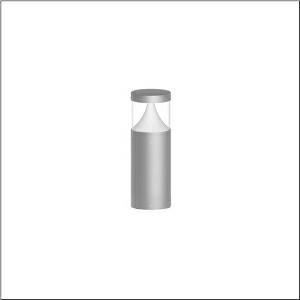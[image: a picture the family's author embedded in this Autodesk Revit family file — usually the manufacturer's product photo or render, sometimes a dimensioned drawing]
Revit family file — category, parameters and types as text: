
# Revit family: cl_31_poller_40_5cl424603
name_source: partatom
category: Lighting Fixtures
units: mm (PartAtom-declared; Revit-internal decimal feet)

## family parameters
Cut with Voids When Loaded = No
Host = Face
Light Source = No
Part Type = Normal
Room Calculation Point = No
Round Connector Dimension = Use Diameter
Shared = No

## types (1)
- --- (1 x LED, 800 lm, 7.2 W, 3000K)
    Apparent Load = 7 VA
    CIE Flux Codes = 19 66 88 92 100
    Color Rendering = 80
    Color Temperature = 3000K
    Default Elevation = 1800 mm
    Description = CL 31 Bollard 40, bollard luminaire, primary light control with lens, of PC, primary optical cover: cover panel, of PC, transparent, secondary light control with reflector, of PC, primary light characteristic: asymmetric, LED, rated luminous flux: 800lm, luminous efficacy: 110lm/W, light colour: 830, colour temperature: 3000K, control gear: ECG DALI, with terminal, 5-pole, max. 2.5mm², mains connection: 220..240V, AC, 50/60Hz, rated input power: 7.2W, luminaire housing, of aluminium, powder-coated, Siteco® metallic grey, diameter: 170mm, height: 400mm, protection rating (complete): IP65, insulation class (complete): insulation class I (protective earthing), certification: CE, ENEC, impact resistance: IK10, permissible operating ambient temperature for outdoor applications: -20..+50°C, packaging unit: 1 piece
    Height = 200 mm  [stored 0.656168 ft]
    Lamp = 1 x LED
    Lamp Light Flux = 800 lm
    Lamp Power = 7.2 W
    Lamp count = 1
    Length = 170 mm  [stored 0.557743 ft]
    Luminous efficacy = 111 lm/W
    Manufacturer = Siteco
    ModVariant = No
    Model = 5CL424603
    Mounting Place = Floor
    Mounting Type = Freestanding
    Number of Poles = 1
    OnlyDefault = Yes
    Power Factor = 1
    Product Name = CL 31 Poller 40
    Product group = bollard luminaire | freestanding
    ProductGroupID = 1303
    Protection Class = Protection class I
    Protection Degree = IP 65
    RLX_Detail_Level = 1
    RlxData = <blob elided: 62537 chars, md5=5da18ba3>
    Socket = socket
    Standby Power = 0 W
    System Light Flux = 800 lm
    System Power = 7 W
    Type Comments = factory setting: luminous flux: 100 % | dim-lin: 254 | 182 mA
    Type Image = l_1006907.jpg
    URL = http://relux.com
    VarID = @adj_117045
    Voltage = 0 V
    Weight = 0.00 kg
    Width = 0 mm  [stored 0 ft]

note: [stored X ft] marks values corroborated as IEEE doubles in the binary element streams (Revit-internal decimal feet)

## geometry (parser evidence)
native form markers: Blend x4, Sweep x15
no freeform markers — native parametric forms only
